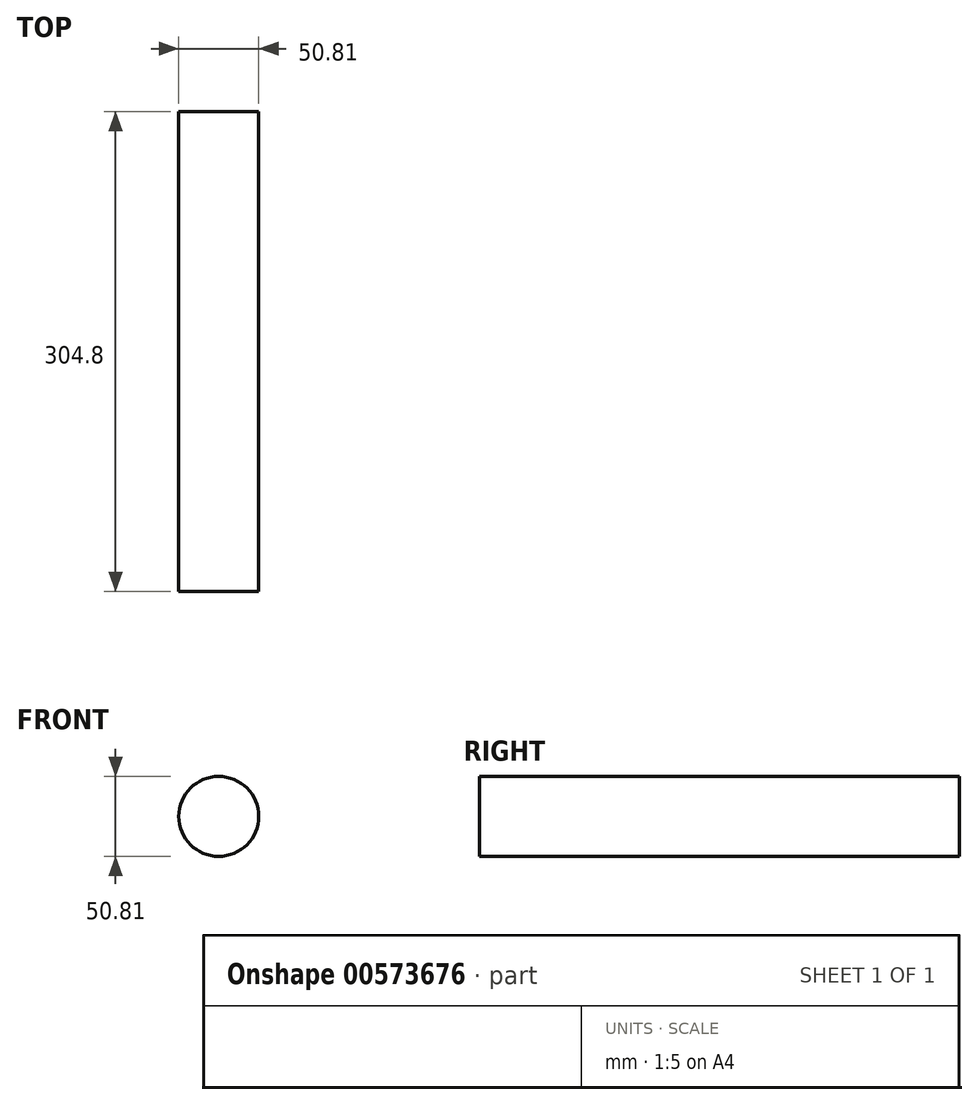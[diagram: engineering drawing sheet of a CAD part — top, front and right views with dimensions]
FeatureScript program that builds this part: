
annotation { "Feature Type Name" : "Feature", "Feature Type Description" : "" }
export const myFeature = defineFeature(function(context is Context, id is Id, definition is map)
    precondition{}
    {
        {
            var Q0;
            Q0=qCreatedBy(makeId("Front.planeOp"),FACE);
            var sketch = newSketch(context, id + "F0", { "sketchPlane" : qUnion([Q0])});
            skPoint(sketch, "E0", {"position": v(-56.92, 37.86) * mm});
            skCircle(sketch, "E1", {"center": v(-56.92, 37.86) * mm, "radius": 25.4 * mm});
            skSolve(sketch);
        }
        {
            var Q0;
            Q0=makeQuery(id+"F0.imprint","IMPRINT",FACE,{"disambiguationData":[TD([[makeQuery(id+"F0.imprint","IMPRINT",EDGE,{"derivedFrom":sQuery(id+"F0.wireOp",EDGE,"E1")}),1.0]])]});
            extrude(context, id + "F1", {"entities" : qUnion([Q0]), "depth" : 304.8 * mm, "offsetDistance" : 25.4 * mm});
        }
    });
